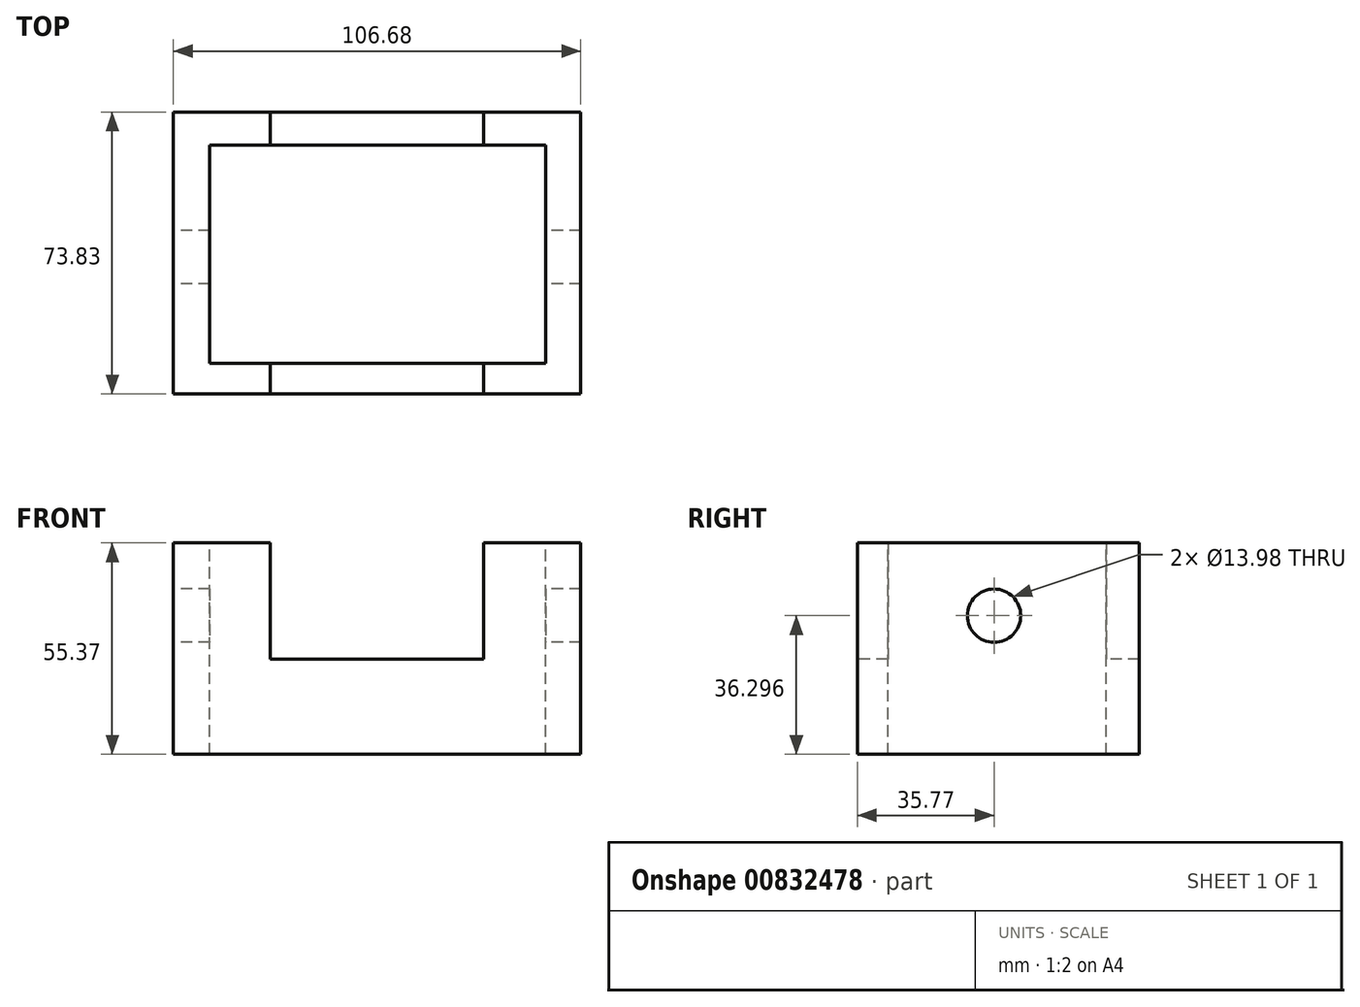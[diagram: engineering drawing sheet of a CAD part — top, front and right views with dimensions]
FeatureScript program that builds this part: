
annotation { "Feature Type Name" : "Feature", "Feature Type Description" : "" }
export const myFeature = defineFeature(function(context is Context, id is Id, definition is map)
    precondition{}
    {
        {
            var Q0;
            Q0=qCreatedBy(makeId("Top.planeOp"),FACE);
            var sketch = newSketch(context, id + "F0", { "sketchPlane" : qUnion([Q0])});
            skLineSegment(sketch, "E0.bottom", {"start": v(-51.3, 38.06) * mm, "end": v(55.37, 38.06) * mm});
            skLineSegment(sketch, "E0.top", {"start": v(-51.3, -35.77) * mm, "end": v(55.37, -35.77) * mm});
            skLineSegment(sketch, "E0.left", {"start": v(-51.3, 38.06) * mm, "end": v(-51.3, -35.77) * mm});
            skLineSegment(sketch, "E0.right", {"start": v(55.37, 38.06) * mm, "end": v(55.37, -35.77) * mm});
            skSolve(sketch);
        }
        {
            var Q0;
            Q0 = qSketchRegion(id + "F0", true);
            extrude(context, id + "F1", {"entities" : qUnion([Q0]), "depth" : 55.37 * mm, "offsetDistance" : 25.4 * mm});
        }
        {
            var Q0;
            Q0=makeQuery(id+"F1.opExtrude","CAP_FACE",FACE,{"disambiguationData":[OSD([sQuery(id+"F0.wireOp",EDGE,"E0.bottom"),sQuery(id+"F0.wireOp",EDGE,"E0.top"),sQuery(id+"F0.wireOp",EDGE,"E0.left"),sQuery(id+"F0.wireOp",EDGE,"E0.right")])],"isStart":false});
            var sketch = newSketch(context, id + "F2", { "sketchPlane" : qUnion([Q0])});
            skLineSegment(sketch, "E1.bottom", {"start": v(-41.77, 29.4) * mm, "end": v(46.19, 29.4) * mm});
            skLineSegment(sketch, "E1.top", {"start": v(-41.77, -27.82) * mm, "end": v(46.19, -27.82) * mm});
            skLineSegment(sketch, "E1.left", {"start": v(-41.77, 29.4) * mm, "end": v(-41.77, -27.82) * mm});
            skLineSegment(sketch, "E1.right", {"start": v(46.19, 29.4) * mm, "end": v(46.19, -27.82) * mm});
            skSolve(sketch);
        }
        {
            var Q0;
            Q0 = qSketchRegion(id + "F2", true);
            extrude(context, id + "F3", {"entities" : qUnion([Q0]), "operationType" : NewBodyOperationType.REMOVE, "oppositeDirection" : true, "depth" : 57.15 * mm, "offsetDistance" : 25.4 * mm});
        }
        {
            var Q0;
            Q0=makeQuery(id+"F1.opExtrude","SWEPT_FACE",FACE,{"disambiguationData":[OSD([sQuery(id+"F0.wireOp",EDGE,"E0.top")])]});
            var sketch = newSketch(context, id + "F4", { "sketchPlane" : qUnion([Q0])});
            skLineSegment(sketch, "E2.bottom", {"start": v(-25.9, 55.37) * mm, "end": v(29.97, 55.37) * mm});
            skLineSegment(sketch, "E2.top", {"start": v(-25.9, 24.9) * mm, "end": v(29.97, 24.9) * mm});
            skLineSegment(sketch, "E2.left", {"start": v(-25.9, 55.37) * mm, "end": v(-25.9, 24.9) * mm});
            skLineSegment(sketch, "E2.right", {"start": v(29.97, 55.37) * mm, "end": v(29.97, 24.9) * mm});
            skSolve(sketch);
        }
        {
            var Q0;
            Q0 = qSketchRegion(id + "F4", true);
            extrude(context, id + "F5", {"entities" : qUnion([Q0]), "operationType" : NewBodyOperationType.REMOVE, "oppositeDirection" : true, "depth" : 75.44 * mm, "offsetDistance" : 25.4 * mm});
        }
        {
            var Q0;
            Q0=makeQuery(id+"F1.opExtrude","SWEPT_FACE",FACE,{"disambiguationData":[OSD([sQuery(id+"F0.wireOp",EDGE,"E0.left")])]});
            var sketch = newSketch(context, id + "F6", { "sketchPlane" : qUnion([Q0])});
            skCircle(sketch, "E3", {"center": v(0, 36.3) * mm, "radius": 7 * mm});
            skSolve(sketch);
        }
        {
            var Q0;
            Q0 = qSketchRegion(id + "F6", true);
            extrude(context, id + "F7", {"entities" : qUnion([Q0]), "operationType" : NewBodyOperationType.REMOVE, "oppositeDirection" : true, "depth" : 111.25 * mm, "offsetDistance" : 25.4 * mm});
        }
    });
